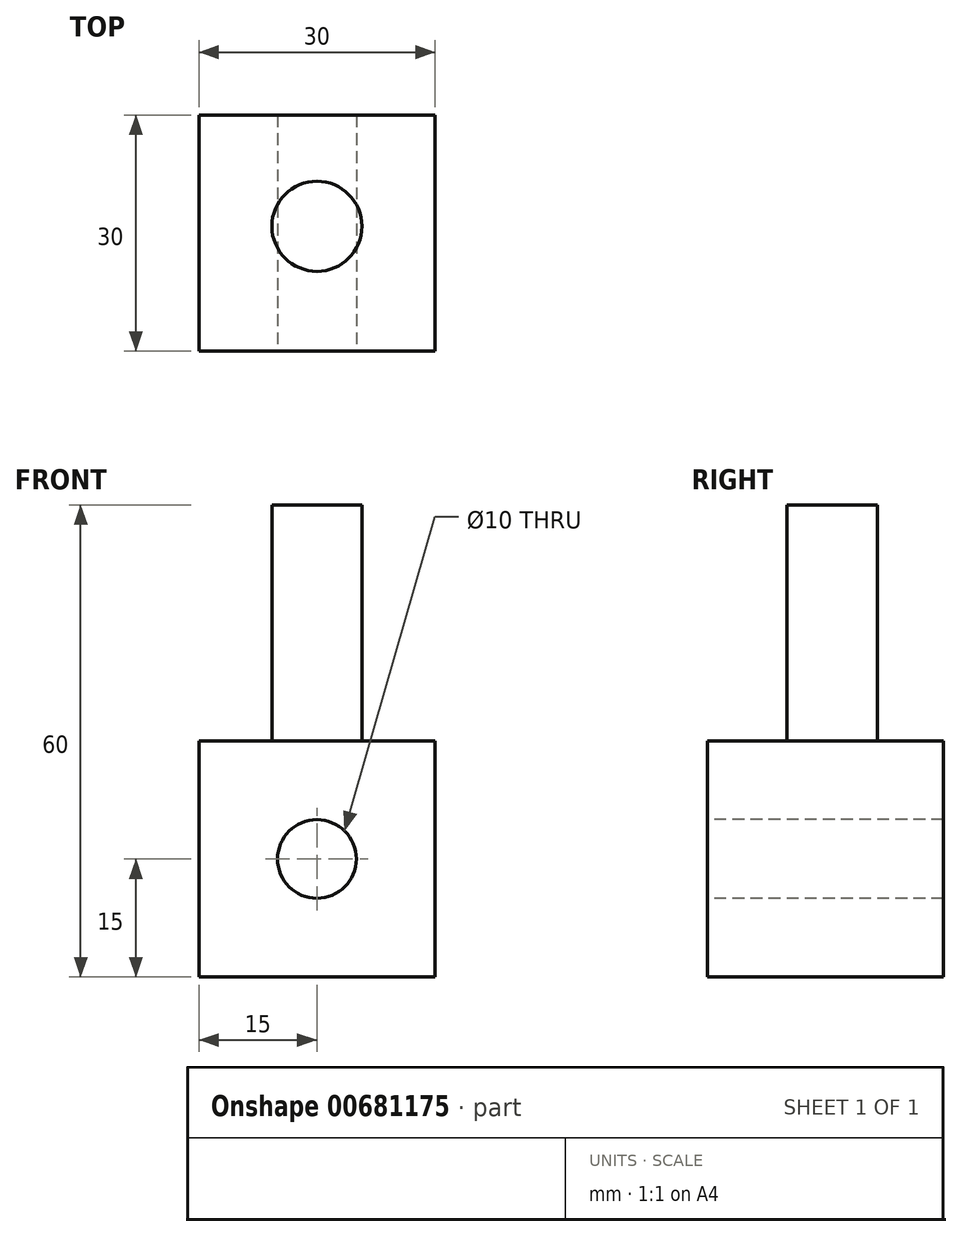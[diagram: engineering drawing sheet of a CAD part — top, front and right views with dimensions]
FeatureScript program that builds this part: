
annotation { "Feature Type Name" : "Feature", "Feature Type Description" : "" }
export const myFeature = defineFeature(function(context is Context, id is Id, definition is map)
    precondition{}
    {
        {
            var Q0;
            Q0=qCreatedBy(makeId("Front.planeOp"),FACE);
            var sketch = newSketch(context, id + "F0", { "sketchPlane" : qUnion([Q0])});
            skLineSegment(sketch, "E0.bottom", {"start": v(15, 15) * mm, "end": v(-15, 15) * mm});
            skLineSegment(sketch, "E0.top", {"start": v(15, -15) * mm, "end": v(-15, -15) * mm});
            skLineSegment(sketch, "E0.left", {"start": v(15, 15) * mm, "end": v(15, -15) * mm});
            skLineSegment(sketch, "E0.right", {"start": v(-15, 15) * mm, "end": v(-15, -15) * mm});
            skPoint(sketch, "E0.middle", {"position": v(0, 0) * mm});
            skSolve(sketch);
        }
        {
            var Q0;
            Q0 = qSketchRegion(id + "F0", true);
            extrude(context, id + "F1", {"entities" : qUnion([Q0]), "oppositeDirection" : true, "depth" : 30 * mm, "offsetDistance" : 25 * mm});
        }
        {
            var Q0;
            Q0=makeQuery(id+"F1.opExtrude","CAP_FACE",FACE,{"disambiguationData":[OSD([sQuery(id+"F0.wireOp",EDGE,"E0.bottom"),sQuery(id+"F0.wireOp",EDGE,"E0.top"),sQuery(id+"F0.wireOp",EDGE,"E0.left"),sQuery(id+"F0.wireOp",EDGE,"E0.right")])],"isStart":true});
            var sketch = newSketch(context, id + "F2", { "sketchPlane" : qUnion([Q0])});
            skCircle(sketch, "E1", {"center": v(0, 0) * mm, "radius": 5 * mm});
            skSolve(sketch);
        }
        {
            var Q0;
            Q0=makeQuery(id+"F2.imprint","IMPRINT",FACE,{"disambiguationData":[TD([[makeQuery(id+"F2.imprint","IMPRINT",EDGE,{"derivedFrom":sQuery(id+"F2.wireOp",EDGE,"E1")}),1.0]])]});
            extrude(context, id + "F3", {"entities" : qUnion([Q0]), "operationType" : NewBodyOperationType.REMOVE, "oppositeDirection" : true, "depth" : 30 * mm, "offsetDistance" : 25 * mm});
        }
        {
            var Q0;
            Q0=makeQuery(id+"F1.opExtrude","SWEPT_FACE",FACE,{"disambiguationData":[OSD([sQuery(id+"F0.wireOp",EDGE,"E0.bottom")])]});
            var sketch = newSketch(context, id + "F4", { "sketchPlane" : qUnion([Q0])});
            skCircle(sketch, "E2", {"center": v(0, 15.87) * mm, "radius": 5.72 * mm});
            skSolve(sketch);
        }
        {
            var Q0;
            Q0=makeQuery(id+"F4.imprint","IMPRINT",FACE,{"disambiguationData":[TD([[makeQuery(id+"F4.imprint","IMPRINT",EDGE,{"derivedFrom":sQuery(id+"F4.wireOp",EDGE,"E2")}),1.0]])]});
            extrude(context, id + "F5", {"entities" : qUnion([Q0]), "operationType" : NewBodyOperationType.ADD, "depth" : 30 * mm, "offsetDistance" : 25 * mm});
        }
    });
